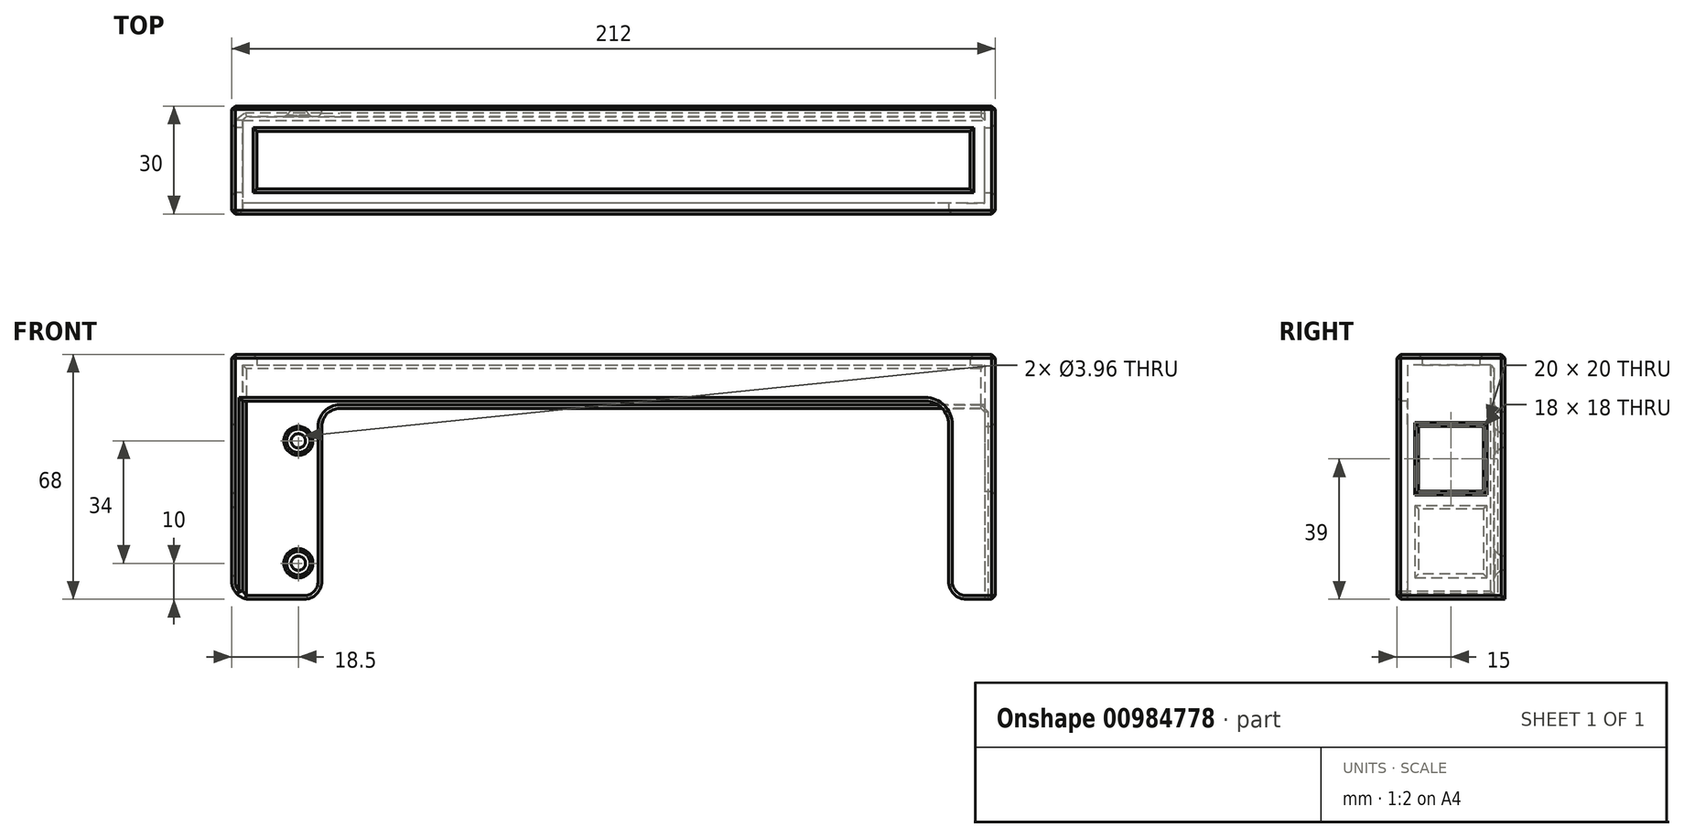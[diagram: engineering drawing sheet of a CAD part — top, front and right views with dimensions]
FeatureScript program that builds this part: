
annotation { "Feature Type Name" : "Feature", "Feature Type Description" : "" }
export const myFeature = defineFeature(function(context is Context, id is Id, definition is map)
    precondition{}
    {
        {
            var Q0;
            Q0=qCreatedBy(makeId("Top.planeOp"),FACE);
            var sketch = newSketch(context, id + "F0", { "sketchPlane" : qUnion([Q0])});
            skLineSegment(sketch, "E0.bottom", {"start": v(-106, -15) * mm, "end": v(106, -15) * mm});
            skLineSegment(sketch, "E0.top", {"start": v(-106, 15) * mm, "end": v(106, 15) * mm});
            skLineSegment(sketch, "E0.left", {"start": v(-106, -15) * mm, "end": v(-106, 15) * mm});
            skLineSegment(sketch, "E0.right", {"start": v(106, -15) * mm, "end": v(106, 15) * mm});
            skPoint(sketch, "E0.middle", {"position": v(0, 0) * mm});
            skLineSegment(sketch, "E1.bottom", {"start": v(103, -12) * mm, "end": v(-103, -12) * mm});
            skLineSegment(sketch, "E1.top", {"start": v(103, 12) * mm, "end": v(-103, 12) * mm});
            skLineSegment(sketch, "E1.left", {"start": v(103, -12) * mm, "end": v(103, 12) * mm});
            skLineSegment(sketch, "E1.right", {"start": v(-103, -12) * mm, "end": v(-103, 12) * mm});
            skLineSegment(sketch, "E2.bottom", {"start": v(0, 0) * mm, "end": v(0, 0) * mm});
            skLineSegment(sketch, "E2.top", {"start": v(0, -39.97) * mm, "end": v(0, -39.97) * mm});
            skLineSegment(sketch, "E2.left", {"start": v(0, 0) * mm, "end": v(0, -39.97) * mm});
            skLineSegment(sketch, "E2.right", {"start": v(0, 0) * mm, "end": v(0, -39.97) * mm});
            skPoint(sketch, "E2.middle", {"position": v(0, -19.98) * mm});
            skLineSegment(sketch, "E3.bottom", {"start": v(-99, -8) * mm, "end": v(99, -8) * mm});
            skLineSegment(sketch, "E3.top", {"start": v(-99, 8) * mm, "end": v(99, 8) * mm});
            skLineSegment(sketch, "E3.left", {"start": v(-99, -8) * mm, "end": v(-99, 8) * mm});
            skLineSegment(sketch, "E3.right", {"start": v(99, -8) * mm, "end": v(99, 8) * mm});
            skLineSegment(sketch, "E4.bottom", {"start": v(99, -8) * mm, "end": v(96, -8) * mm});
            skLineSegment(sketch, "E4.top", {"start": v(99, 8) * mm, "end": v(96, 8) * mm});
            skLineSegment(sketch, "E4.right", {"start": v(96, -8) * mm, "end": v(96, 8) * mm});
            skLineSegment(sketch, "E5", {"start": v(96, -8) * mm, "end": v(63, -8) * mm});
            skLineSegment(sketch, "E6.bottom", {"start": v(63, -8) * mm, "end": v(60, -8) * mm});
            skLineSegment(sketch, "E6.top", {"start": v(63, 8) * mm, "end": v(60, 8) * mm});
            skLineSegment(sketch, "E6.left", {"start": v(63, -8) * mm, "end": v(63, 8) * mm});
            skLineSegment(sketch, "E6.right", {"start": v(60, -8) * mm, "end": v(60, 8) * mm});
            skLineSegment(sketch, "E7", {"start": v(60, -8) * mm, "end": v(-36, -8) * mm});
            skLineSegment(sketch, "E8.bottom", {"start": v(-36, -8) * mm, "end": v(-70, -8) * mm});
            skLineSegment(sketch, "E8.top", {"start": v(-36, 8) * mm, "end": v(-70, 8) * mm});
            skLineSegment(sketch, "E8.left", {"start": v(-36, -8) * mm, "end": v(-36, 8) * mm});
            skLineSegment(sketch, "E8.right", {"start": v(-70, -8) * mm, "end": v(-70, 8) * mm});
            skLineSegment(sketch, "E9.bottom", {"start": v(-99, -8) * mm, "end": v(-85, -8) * mm});
            skLineSegment(sketch, "E9.top", {"start": v(-99, 8) * mm, "end": v(-85, 8) * mm});
            skLineSegment(sketch, "E9.right", {"start": v(-85, -8) * mm, "end": v(-85, 8) * mm});
            skSolve(sketch);
        }
        {
            var Q0;
            Q0=makeQuery(id+"F0.imprint","IMPRINT",FACE,{"disambiguationData":[TD([[makeQuery(id+"F0.imprint","IMPRINT",EDGE,{"derivedFrom":sQuery(id+"F0.wireOp",EDGE,"E0.top")}),-1.0]])]});
            var Q1;
            Q1=makeQuery(id+"F0.imprint","IMPRINT",FACE,{"disambiguationData":[TD([[makeQuery(id+"F0.imprint","IMPRINT",EDGE,{"derivedFrom":sQuery(id+"F0.wireOp",EDGE,"E1.top")}),1.0]])]});
            var Q2;
            Q2=makeQuery(id+"F0.imprint","IMPRINT",FACE,{"disambiguationData":[TD([[makeQuery(id+"F0.imprint","IMPRINT",EDGE,{"derivedFrom":sQuery(id+"F0.wireOp",EDGE,"E6.bottom")}),-1.0]])]});
            var Q3;
            Q3=makeQuery(id+"F0.imprint","IMPRINT",FACE,{"disambiguationData":[TD([[makeQuery(id+"F0.imprint","IMPRINT",EDGE,{"derivedFrom":sQuery(id+"F0.wireOp",EDGE,"E8.bottom")}),-1.0]])]});
            var Q4;
            Q4=makeQuery(id+"F0.imprint","IMPRINT",FACE,{"disambiguationData":[TD([[makeQuery(id+"F0.imprint","IMPRINT",EDGE,{"derivedFrom":sQuery(id+"F0.wireOp",EDGE,"E9.bottom")}),1.0]])]});
            var Q5;
            Q5=makeQuery(id+"F0.imprint","IMPRINT",FACE,{"disambiguationData":[TD([[makeQuery(id+"F0.imprint","IMPRINT",EDGE,{"derivedFrom":sQuery(id+"F0.wireOp",EDGE,"E4.bottom")}),-1.0]])]});
            extrude(context, id + "F1", {"entities" : qUnion([Q0, Q1, Q2, Q3, Q4, Q5]), "depth" : 3 * mm, "offsetDistance" : 25 * mm});
        }
        {
            var Q0;
            Q0=makeQuery(id+"F1.opExtrude","SWEPT_FACE",FACE,{"disambiguationData":[OSD([sQuery(id+"F0.wireOp",EDGE,"E0.bottom")])]});
            var sketch = newSketch(context, id + "F2", { "sketchPlane" : qUnion([Q0])});
            skLineSegment(sketch, "E10.bottom", {"start": v(-103, 0) * mm, "end": v(103, 0) * mm});
            skLineSegment(sketch, "E10.top", {"start": v(-103, -65) * mm, "end": v(103, -65) * mm});
            skLineSegment(sketch, "E10.left", {"start": v(-103, 0) * mm, "end": v(-103, -65) * mm});
            skLineSegment(sketch, "E10.right", {"start": v(103, 0) * mm, "end": v(103, -65) * mm});
            skLineSegment(sketch, "E11.bottom", {"start": v(-103, 0) * mm, "end": v(-92.5, 0) * mm});
            skLineSegment(sketch, "E11.top", {"start": v(-103, -65) * mm, "end": v(-93, -65) * mm});
            skLineSegment(sketch, "E11.right", {"start": v(-93, -16.41) * mm, "end": v(-93, -65) * mm});
            skLineSegment(sketch, "E12.top", {"start": v(-86.57, -9.98) * mm, "end": v(103, -9.98) * mm});
            skLineSegment(sketch, "E12.left", {"start": v(-103, 0) * mm, "end": v(-103, -10) * mm});
            skLineSegment(sketch, "E12.right", {"start": v(103, 0) * mm, "end": v(103, -9.98) * mm});
            skPoint(sketch, "E13.newPointB", {"position": v(-93, 0) * mm});
            skArc(sketch, "E13.filletArc", {"start": v(-86.57, -9.98) * mm, "mid": v(-91.12, -11.87) * mm, "end": v(-93, -16.41) * mm});
            skArc(sketch, "E14.MirrorCS", {"start": v(86.57, -9.98) * mm, "mid": v(91.12, -11.87) * mm, "end": v(93, -16.41) * mm});
            skLineSegment(sketch, "E15.MirrorCS", {"start": v(86.57, -9.98) * mm, "end": v(-103, -9.98) * mm});
            skLineSegment(sketch, "E16.MirrorCS", {"start": v(93, -16.41) * mm, "end": v(93, -65) * mm});
            skSolve(sketch);
        }
        {
            var Q0;
            Q0=makeQuery(id+"F1.opExtrude","SWEPT_FACE",FACE,{"disambiguationData":[OSD([sQuery(id+"F0.wireOp",EDGE,"E0.bottom")])]});
            var Q1;
            Q1=makeQuery(id+"F2.imprint","IMPRINT",FACE,{"disambiguationData":[TD([[makeQuery(id+"F2.imprint","IMPRINT",EDGE,{"derivedFrom":sQuery(id+"F2.wireOp",EDGE,"E11.top")}),1.0]])]});
            var Q2;
            {var subQ1=sQuery(id+"F2.wireOp",EDGE,"E12.top");Q2=makeQuery(id+"F2.imprint","IMPRINT",FACE,{"disambiguationData":[TD([[makeQuery(id+"F2.imprint","IMPRINT",EDGE,{"derivedFrom":subQ1}),1.0]])]});}
            var Q3;
            {var subQ0=sQuery(id+"F2.wireOp",EDGE,"E10.right");Q3=makeQuery(id+"F2.imprint","IMPRINT",FACE,{"disambiguationData":[TD([[makeQuery(id+"F2.imprint","IMPRINT",EDGE,{"derivedFrom":subQ0}),-1.0]])]});}
            extrude(context, id + "F3", {"entities" : qUnion([Q0, Q1, Q2, Q3]), "operationType" : NewBodyOperationType.ADD, "oppositeDirection" : true, "depth" : 3 * mm, "offsetDistance" : 25 * mm});
        }
        {
            var Q0;
            Q0=makeQuery(id+"F1.opExtrude","SWEPT_FACE",FACE,{"disambiguationData":[OSD([sQuery(id+"F0.wireOp",EDGE,"E0.top")])]});
            var sketch = newSketch(context, id + "F4", { "sketchPlane" : qUnion([Q0])});
            skLineSegment(sketch, "E17.bottom", {"start": v(-106, 0) * mm, "end": v(106, 0) * mm});
            skLineSegment(sketch, "E17.top", {"start": v(-106, -65) * mm, "end": v(106, -65) * mm});
            skLineSegment(sketch, "E17.left", {"start": v(-106, 0) * mm, "end": v(-106, -65) * mm});
            skLineSegment(sketch, "E17.right", {"start": v(106, 0) * mm, "end": v(106, -65) * mm});
            skLineSegment(sketch, "E18.bottom", {"start": v(-106, 0) * mm, "end": v(-77.5, 0) * mm});
            skLineSegment(sketch, "E18.top", {"start": v(-106, -65) * mm, "end": v(-81, -65) * mm});
            skLineSegment(sketch, "E18.right", {"start": v(-81, -17) * mm, "end": v(-81, -65) * mm});
            skLineSegment(sketch, "E19.bottom", {"start": v(-106, 3) * mm, "end": v(106, 3) * mm});
            skLineSegment(sketch, "E19.top", {"start": v(-76, -12) * mm, "end": v(106, -12) * mm});
            skLineSegment(sketch, "E19.left", {"start": v(-106, 3) * mm, "end": v(-106, -22) * mm});
            skLineSegment(sketch, "E19.right", {"start": v(106, 3) * mm, "end": v(106, -12) * mm});
            skPoint(sketch, "E20.newPointB", {"position": v(-81, 0) * mm});
            skArc(sketch, "E20.filletArc", {"start": v(-76, -12) * mm, "mid": v(-79.54, -13.46) * mm, "end": v(-81, -17) * mm});
            skArc(sketch, "E21.MirrorCS", {"start": v(76, -12) * mm, "mid": v(79.54, -13.46) * mm, "end": v(81, -17) * mm});
            skLineSegment(sketch, "E22.MirrorCS", {"start": v(76, -12) * mm, "end": v(-106, -12) * mm});
            skLineSegment(sketch, "E23.MirrorCS", {"start": v(81, -17) * mm, "end": v(81, -65) * mm});
            skSolve(sketch);
        }
        {
            var Q0;
            {var subQ5=sQuery(id+"F4.wireOp",EDGE,"E17.bottom");Q0=makeQuery(id+"F4.imprint","IMPRINT",FACE,{"disambiguationData":[TD([[makeQuery(id+"F4.imprint","IMPRINT",EDGE,{"derivedFrom":subQ5}),1.0]])]});}
            var Q1;
            {var subQ2=sQuery(id+"F4.wireOp",EDGE,"E18.top");Q1=makeQuery(id+"F4.imprint","IMPRINT",FACE,{"disambiguationData":[TD([[makeQuery(id+"F4.imprint","IMPRINT",EDGE,{"derivedFrom":subQ2}),1.0]])]});}
            var Q2;
            {var subQ0=sQuery(id+"F4.wireOp",EDGE,"E19.top");Q2=makeQuery(id+"F4.imprint","IMPRINT",FACE,{"disambiguationData":[TD([[makeQuery(id+"F4.imprint","IMPRINT",EDGE,{"derivedFrom":subQ0}),-1.0]])]});}
            var Q3;
            {var subQ3=sQuery(id+"F4.wireOp",EDGE,"E17.bottom");Q3=makeQuery(id+"F4.imprint","IMPRINT",FACE,{"disambiguationData":[TD([[makeQuery(id+"F4.imprint","IMPRINT",EDGE,{"derivedFrom":subQ3}),-1.0]])]});}
            extrude(context, id + "F5", {"entities" : qUnion([Q0, Q1, Q2, Q3]), "operationType" : NewBodyOperationType.ADD, "oppositeDirection" : true, "depth" : 3 * mm, "offsetDistance" : 25 * mm});
        }
        {
            var Q0;
            Q0=makeQuery(id+"F5.opExtrude","CAP_FACE",FACE,{"disambiguationData":[OSD([sQuery(id+"F4.wireOp",EDGE,"E17.top"),sQuery(id+"F4.wireOp",EDGE,"E17.right"),sQuery(id+"F4.wireOp",EDGE,"E18.top"),sQuery(id+"F4.wireOp",EDGE,"E17.left"),sQuery(id+"F4.wireOp",EDGE,"E18.right"),sQuery(id+"F4.wireOp",EDGE,"E19.bottom"),sQuery(id+"F4.wireOp",EDGE,"E19.left"),sQuery(id+"F4.wireOp",EDGE,"E19.right"),sQuery(id+"F4.wireOp",EDGE,"E20.filletArc"),sQuery(id+"F4.wireOp",EDGE,"E21.MirrorCS"),sQuery(id+"F4.wireOp",EDGE,"E22.MirrorCS"),sQuery(id+"F4.wireOp",EDGE,"E23.MirrorCS")])],"isStart":false});
            var sketch = newSketch(context, id + "F6", { "sketchPlane" : qUnion([Q0])});
            skLineSegment(sketch, "E24.bottom", {"start": v(0, 0) * mm, "end": v(87.5, 0) * mm});
            skLineSegment(sketch, "E24.top", {"start": v(0, -65) * mm, "end": v(87.5, -65) * mm});
            skLineSegment(sketch, "E24.left", {"start": v(0, 0) * mm, "end": v(0, -65) * mm});
            skLineSegment(sketch, "E24.right", {"start": v(87.5, 0) * mm, "end": v(87.5, -65) * mm});
            skLineSegment(sketch, "E25", {"start": v(87.5, 0) * mm, "end": v(87.5, -21) * mm});
            skLineSegment(sketch, "E26", {"start": v(87.5, -65) * mm, "end": v(87.5, -55) * mm});
            skLineSegment(sketch, "E27.MirrorCS", {"start": v(-87.5, 0) * mm, "end": v(-87.5, -65) * mm});
            skLineSegment(sketch, "E28.MirrorCS", {"start": v(-87.5, 0) * mm, "end": v(-87.5, -21) * mm});
            skLineSegment(sketch, "E29.MirrorCS", {"start": v(-87.5, -65) * mm, "end": v(-87.5, -55) * mm});
            skSolve(sketch);
        }
        {
            var Q0;
            Q0=sQuery(id+"F6.wireOp",VERTEX,"E26.end");
            var Q1;
            Q1=sQuery(id+"F6.wireOp",VERTEX,"E25.end");
            var Q2;
            Q2=sQuery(id+"F6.wireOp",VERTEX,"E28.MirrorCS.end");
            var Q3;
            Q3=sQuery(id+"F6.wireOp",VERTEX,"E29.MirrorCS.end");
            var Q4;
            Q4=makeQuery(id+"F1.opExtrude","SWEPT_BODY",BODY,{"disambiguationData":[OSD([sQuery(id+"F0.wireOp",EDGE,"E0.bottom"),sQuery(id+"F0.wireOp",EDGE,"E0.top"),sQuery(id+"F0.wireOp",EDGE,"E0.left"),sQuery(id+"F0.wireOp",EDGE,"E0.right"),sQuery(id+"F0.wireOp",EDGE,"E1.bottom"),sQuery(id+"F0.wireOp",EDGE,"E1.top"),sQuery(id+"F0.wireOp",EDGE,"E1.left"),sQuery(id+"F0.wireOp",EDGE,"E1.right")])]});
            hole(context, id + "F7", {"style" : HoleStyle.C_SINK, "endStyle" : HoleEndStyle.THROUGH, "standardTappedOrClearance" : lookupTablePath({ "fit" : "Normal (ASME)", "standard" : "ANSI", "size" : "#5", "type" : "Clearance" }), "standardBlindInLast" : lookupTablePath({ "fit" : "Normal", "standard" : "ANSI", "engagement" : "75%", "pitch" : "40 tpi", "size" : "#5", "type" : "Clearance & tapped" }), "holeDiameter" : 3.96 * mm, "cSinkDiameter" : 7.14 * mm, "cSinkAngle" : 82 * degree, "majorDiameter" : 5 * mm, "isTappedThrough" : true, "tappedDepth" : 12 * mm, "tapClearance" : 3, "locations" : qUnion([Q0, Q1, Q2, Q3]), "scope" : qUnion([Q4])});
        }
        {
            var Q0;
            Q0=makeQuery(id+"F1.opExtrude","SWEPT_FACE",FACE,{"disambiguationData":[OSD([sQuery(id+"F0.wireOp",EDGE,"E0.left")])]});
            var sketch = newSketch(context, id + "F8", { "sketchPlane" : qUnion([Q0])});
            skLineSegment(sketch, "E30.bottom", {"start": v(-15, 0) * mm, "end": v(15, 0) * mm});
            skLineSegment(sketch, "E30.top", {"start": v(-15, -65) * mm, "end": v(15, -65) * mm});
            skLineSegment(sketch, "E30.left", {"start": v(-15, 0) * mm, "end": v(-15, -65) * mm});
            skLineSegment(sketch, "E30.right", {"start": v(15, 0) * mm, "end": v(15, -65) * mm});
            skLineSegment(sketch, "E31", {"start": v(-15, 0) * mm, "end": v(-9, 0) * mm});
            skLineSegment(sketch, "E32", {"start": v(-9, 0) * mm, "end": v(-9, -17) * mm});
            skLineSegment(sketch, "E33.bottom", {"start": v(-9, -17) * mm, "end": v(9, -17) * mm});
            skLineSegment(sketch, "E33.top", {"start": v(-9, -35) * mm, "end": v(9, -35) * mm});
            skLineSegment(sketch, "E33.left", {"start": v(-9, -17) * mm, "end": v(-9, -35) * mm});
            skLineSegment(sketch, "E33.right", {"start": v(9, -17) * mm, "end": v(9, -35) * mm});
            skLineSegment(sketch, "E34", {"start": v(-9, -35) * mm, "end": v(-9, -40) * mm});
            skLineSegment(sketch, "E35.bottom", {"start": v(-9, -40) * mm, "end": v(9, -40) * mm});
            skLineSegment(sketch, "E35.top", {"start": v(-9, -58) * mm, "end": v(9, -58) * mm});
            skLineSegment(sketch, "E35.left", {"start": v(-9, -40) * mm, "end": v(-9, -58) * mm});
            skLineSegment(sketch, "E35.right", {"start": v(9, -40) * mm, "end": v(9, -58) * mm});
            skSolve(sketch);
        }
        {
            var Q0;
            Q0=makeQuery(id+"F8.imprint","IMPRINT",FACE,{"disambiguationData":[TD([[makeQuery(id+"F8.imprint","IMPRINT",EDGE,{"derivedFrom":sQuery(id+"F8.wireOp",EDGE,"E30.bottom")}),1.0]])]});
            var Q1;
            Q1=makeQuery(id+"F8.imprint","IMPRINT",FACE,{"disambiguationData":[TD([[makeQuery(id+"F8.imprint","IMPRINT",EDGE,{"derivedFrom":sQuery(id+"F8.wireOp",EDGE,"E30.bottom")}),-1.0]])]});
            extrude(context, id + "F9", {"entities" : qUnion([Q0, Q1]), "operationType" : NewBodyOperationType.ADD, "oppositeDirection" : true, "depth" : 3 * mm, "offsetDistance" : 25 * mm});
        }
        {
            var Q0;
            {var subQ0=sQuery(id+"F0.wireOp",EDGE,"E0.right");Q0=makeQuery(id+"F5.boolean.opBoolean","MERGE",FACE,{"derivedFrom":[makeQuery(id+"F3.boolean.opBoolean","MERGE",FACE,{"derivedFrom":[makeQuery(id+"F1.opExtrude","SWEPT_FACE",FACE,{"disambiguationData":[OSD([subQ0])]}),makeQuery(id+"F3.opExtrude","SWEPT_FACE",FACE,{"disambiguationData":[OSD([sQuery(id+"F0.wireOp",EDGE,"E0.bottom"),subQ0])]}),makeQuery(id+"F3.opExtrude","SWEPT_FACE",FACE,{"disambiguationData":[OSD([sQuery(id+"F2.wireOp",EDGE,"E10.right"),sQuery(id+"F2.wireOp",EDGE,"E12.right")])]})]}),makeQuery(id+"F5.opExtrude","SWEPT_FACE",FACE,{"disambiguationData":[OSD([sQuery(id+"F4.wireOp",EDGE,"E17.left"),sQuery(id+"F4.wireOp",EDGE,"E19.left")])]})]});}
            var sketch = newSketch(context, id + "F10", { "sketchPlane" : qUnion([Q0])});
            skLineSegment(sketch, "E36", {"start": v(-15, 0) * mm, "end": v(-9, 0) * mm});
            skLineSegment(sketch, "E37", {"start": v(-9, 0) * mm, "end": v(-9, -17) * mm});
            skLineSegment(sketch, "E38.bottom", {"start": v(-15, 0) * mm, "end": v(15, 0) * mm});
            skLineSegment(sketch, "E38.top", {"start": v(-15, -65) * mm, "end": v(15, -65) * mm});
            skLineSegment(sketch, "E38.left", {"start": v(-15, 0) * mm, "end": v(-15, -65) * mm});
            skLineSegment(sketch, "E38.right", {"start": v(15, 0) * mm, "end": v(15, -65) * mm});
            skLineSegment(sketch, "E39.bottom", {"start": v(-9, -17) * mm, "end": v(9, -17) * mm});
            skLineSegment(sketch, "E39.top", {"start": v(-9, -35) * mm, "end": v(9, -35) * mm});
            skLineSegment(sketch, "E39.left", {"start": v(-9, -17) * mm, "end": v(-9, -35) * mm});
            skLineSegment(sketch, "E39.right", {"start": v(9, -17) * mm, "end": v(9, -35) * mm});
            skSolve(sketch);
        }
        {
            var Q0;
            {var subQ1=sQuery(id+"F10.wireOp",EDGE,"E38.left");Q0=makeQuery(id+"F10.imprint","IMPRINT",FACE,{"disambiguationData":[TD([[makeQuery(id+"F10.imprint","IMPRINT",EDGE,{"derivedFrom":subQ1}),-1.0]])]});}
            var Q1;
            Q1=makeQuery(id+"F10.imprint","IMPRINT",FACE,{"disambiguationData":[TD([[makeQuery(id+"F10.imprint","IMPRINT",EDGE,{"derivedFrom":sQuery(id+"F10.wireOp",EDGE,"E38.top")}),1.0]])]});
            var Q2;
            {var subQ0=sQuery(id+"F10.wireOp",EDGE,"E38.left");Q2=makeQuery(id+"F10.imprint","IMPRINT",FACE,{"disambiguationData":[TD([[makeQuery(id+"F10.imprint","IMPRINT",EDGE,{"derivedFrom":subQ0}),1.0]])]});}
            extrude(context, id + "F11", {"entities" : qUnion([Q0, Q1, Q2]), "operationType" : NewBodyOperationType.ADD, "oppositeDirection" : true, "depth" : 3 * mm, "offsetDistance" : 25 * mm});
        }
        {
            var Q0;
            Q0=makeQuery(id+"F3.opExtrude","SWEPT_EDGE",EDGE,{"disambiguationData":[OSD([sQuery(id+"F2.wireOp",EDGE,"E10.top"),sQuery(id+"F2.wireOp",EDGE,"E16.MirrorCS")])]});
            var Q1;
            Q1=makeQuery(id+"F5.opExtrude","SWEPT_EDGE",EDGE,{"disambiguationData":[OSD([sQuery(id+"F4.wireOp",EDGE,"E17.top"),sQuery(id+"F4.wireOp",EDGE,"E18.top"),sQuery(id+"F4.wireOp",EDGE,"E18.right")])]});
            var Q2;
            Q2=makeQuery(id+"F5.opExtrude","SWEPT_EDGE",EDGE,{"disambiguationData":[OSD([sQuery(id+"F4.wireOp",EDGE,"E17.top"),sQuery(id+"F4.wireOp",EDGE,"E23.MirrorCS")])]});
            var Q3;
            Q3=makeQuery(id+"F3.opExtrude","SWEPT_EDGE",EDGE,{"disambiguationData":[OSD([sQuery(id+"F2.wireOp",EDGE,"E10.top"),sQuery(id+"F2.wireOp",EDGE,"E11.top"),sQuery(id+"F2.wireOp",EDGE,"E11.right")])]});
            fillet(context, id + "F12", {"entities" : qUnion([Q0, Q1, Q2, Q3]), "radius" : 5 * mm, "tangentPropagation" : true, "allowEdgeOverflow" : false});
        }
        {
            var Q0;
            {var subQ0=sQuery(id+"F4.wireOp",EDGE,"E19.right");var subQ1=sQuery(id+"F4.wireOp",EDGE,"E17.right");var subQ2=sQuery(id+"F0.wireOp",EDGE,"E0.left");Q0=makeQuery(id+"F9.boolean.opBoolean","MERGE",FACE,{"derivedFrom":[makeQuery(id+"F5.boolean.opBoolean","MERGE",FACE,{"derivedFrom":[makeQuery(id+"F1.opExtrude","SWEPT_FACE",FACE,{"disambiguationData":[OSD([subQ2])]}),makeQuery(id+"F5.opExtrude","SWEPT_FACE",FACE,{"disambiguationData":[OSD([subQ1,subQ0])]})]}),makeQuery(id+"F9.opExtrude","CAP_FACE",FACE,{"disambiguationData":[OSD([sQuery(id+"F0.wireOp",EDGE,"E0.bottom"),sQuery(id+"F0.wireOp",EDGE,"E0.top"),subQ2,subQ1,subQ0,sQuery(id+"F8.wireOp",EDGE,"E30.top"),sQuery(id+"F8.wireOp",EDGE,"E30.right"),sQuery(id+"F8.wireOp",EDGE,"E31"),sQuery(id+"F8.wireOp",EDGE,"E33.bottom"),sQuery(id+"F8.wireOp",EDGE,"E33.top"),sQuery(id+"F8.wireOp",EDGE,"E33.left"),sQuery(id+"F8.wireOp",EDGE,"E33.right"),sQuery(id+"F8.wireOp",EDGE,"E35.bottom"),sQuery(id+"F8.wireOp",EDGE,"E35.top"),sQuery(id+"F8.wireOp",EDGE,"E35.left"),sQuery(id+"F8.wireOp",EDGE,"E35.right")])],"isStart":true})]});}
            var Q1;
            Q1=makeQuery(id+"F11.boolean.opBoolean","MERGE",FACE,{"derivedFrom":[makeQuery(id+"F5.boolean.opBoolean","MERGE",FACE,{"derivedFrom":[makeQuery(id+"F1.opExtrude","SWEPT_FACE",FACE,{"disambiguationData":[OSD([sQuery(id+"F0.wireOp",EDGE,"E0.right")])]}),makeQuery(id+"F5.opExtrude","SWEPT_FACE",FACE,{"disambiguationData":[OSD([sQuery(id+"F4.wireOp",EDGE,"E17.left"),sQuery(id+"F4.wireOp",EDGE,"E19.left")])]})]}),makeQuery(id+"F11.opExtrude","CAP_FACE",FACE,{"disambiguationData":[OSD([sQuery(id+"F10.wireOp",EDGE,"E38.bottom"),sQuery(id+"F10.wireOp",EDGE,"E38.top"),sQuery(id+"F10.wireOp",EDGE,"E38.left"),sQuery(id+"F10.wireOp",EDGE,"E38.right"),sQuery(id+"F10.wireOp",EDGE,"E39.bottom"),sQuery(id+"F10.wireOp",EDGE,"E39.top"),sQuery(id+"F10.wireOp",EDGE,"E39.left"),sQuery(id+"F10.wireOp",EDGE,"E39.right")])],"isStart":true})]});
            var Q2;
            {var subQ0=sQuery(id+"F0.wireOp",EDGE,"E0.bottom");Q2=makeQuery(id+"F11.boolean.opBoolean","MERGE",FACE,{"derivedFrom":[makeQuery(id+"F9.boolean.opBoolean","MERGE",FACE,{"derivedFrom":[makeQuery(id+"F3.boolean.opBoolean","MERGE",FACE,{"derivedFrom":[makeQuery(id+"F1.opExtrude","SWEPT_FACE",FACE,{"disambiguationData":[OSD([subQ0])]}),makeQuery(id+"F3.opExtrude","CAP_FACE",FACE,{"disambiguationData":[OSD([subQ0])],"isStart":true}),makeQuery(id+"F3.opExtrude","CAP_FACE",FACE,{"disambiguationData":[OSD([sQuery(id+"F2.wireOp",EDGE,"E10.top"),sQuery(id+"F2.wireOp",EDGE,"E10.right"),sQuery(id+"F2.wireOp",EDGE,"E11.top"),sQuery(id+"F2.wireOp",EDGE,"E10.left"),sQuery(id+"F2.wireOp",EDGE,"E11.right"),sQuery(id+"F2.wireOp",EDGE,"E10.bottom"),sQuery(id+"F2.wireOp",EDGE,"E12.left"),sQuery(id+"F2.wireOp",EDGE,"E12.right"),sQuery(id+"F2.wireOp",EDGE,"E13.filletArc"),sQuery(id+"F2.wireOp",EDGE,"E14.MirrorCS"),sQuery(id+"F2.wireOp",EDGE,"E15.MirrorCS"),sQuery(id+"F2.wireOp",EDGE,"E16.MirrorCS")])],"isStart":true})]}),makeQuery(id+"F9.opExtrude","SWEPT_FACE",FACE,{"disambiguationData":[OSD([subQ0,sQuery(id+"F0.wireOp",EDGE,"E0.left"),sQuery(id+"F8.wireOp",EDGE,"E30.right")])]})]}),makeQuery(id+"F11.opExtrude","SWEPT_FACE",FACE,{"disambiguationData":[OSD([sQuery(id+"F10.wireOp",EDGE,"E38.left")])]})]});}
            var Q3;
            Q3=makeQuery(id+"F5.opExtrude","CAP_FACE",FACE,{"disambiguationData":[OSD([sQuery(id+"F4.wireOp",EDGE,"E17.top"),sQuery(id+"F4.wireOp",EDGE,"E17.right"),sQuery(id+"F4.wireOp",EDGE,"E18.top"),sQuery(id+"F4.wireOp",EDGE,"E17.left"),sQuery(id+"F4.wireOp",EDGE,"E18.right"),sQuery(id+"F4.wireOp",EDGE,"E19.bottom"),sQuery(id+"F4.wireOp",EDGE,"E19.left"),sQuery(id+"F4.wireOp",EDGE,"E19.right"),sQuery(id+"F4.wireOp",EDGE,"E20.filletArc"),sQuery(id+"F4.wireOp",EDGE,"E21.MirrorCS"),sQuery(id+"F4.wireOp",EDGE,"E22.MirrorCS"),sQuery(id+"F4.wireOp",EDGE,"E23.MirrorCS")])],"isStart":false});
            var Q4;
            Q4=makeQuery(id+"F1.opExtrude","CAP_FACE",FACE,{"disambiguationData":[OSD([sQuery(id+"F0.wireOp",EDGE,"E0.bottom"),sQuery(id+"F0.wireOp",EDGE,"E0.top"),sQuery(id+"F0.wireOp",EDGE,"E0.left"),sQuery(id+"F0.wireOp",EDGE,"E0.right"),sQuery(id+"F0.wireOp",EDGE,"E3.bottom"),sQuery(id+"F0.wireOp",EDGE,"E3.top"),sQuery(id+"F0.wireOp",EDGE,"E3.left"),sQuery(id+"F0.wireOp",EDGE,"E3.right")])],"isStart":false});
            chamfer(context, id + "F13", {"entities" : qUnion([Q0, Q1, Q2, Q3, Q4]), "width" : 1 * mm, "tangentPropagation" : true});
        }
    });
